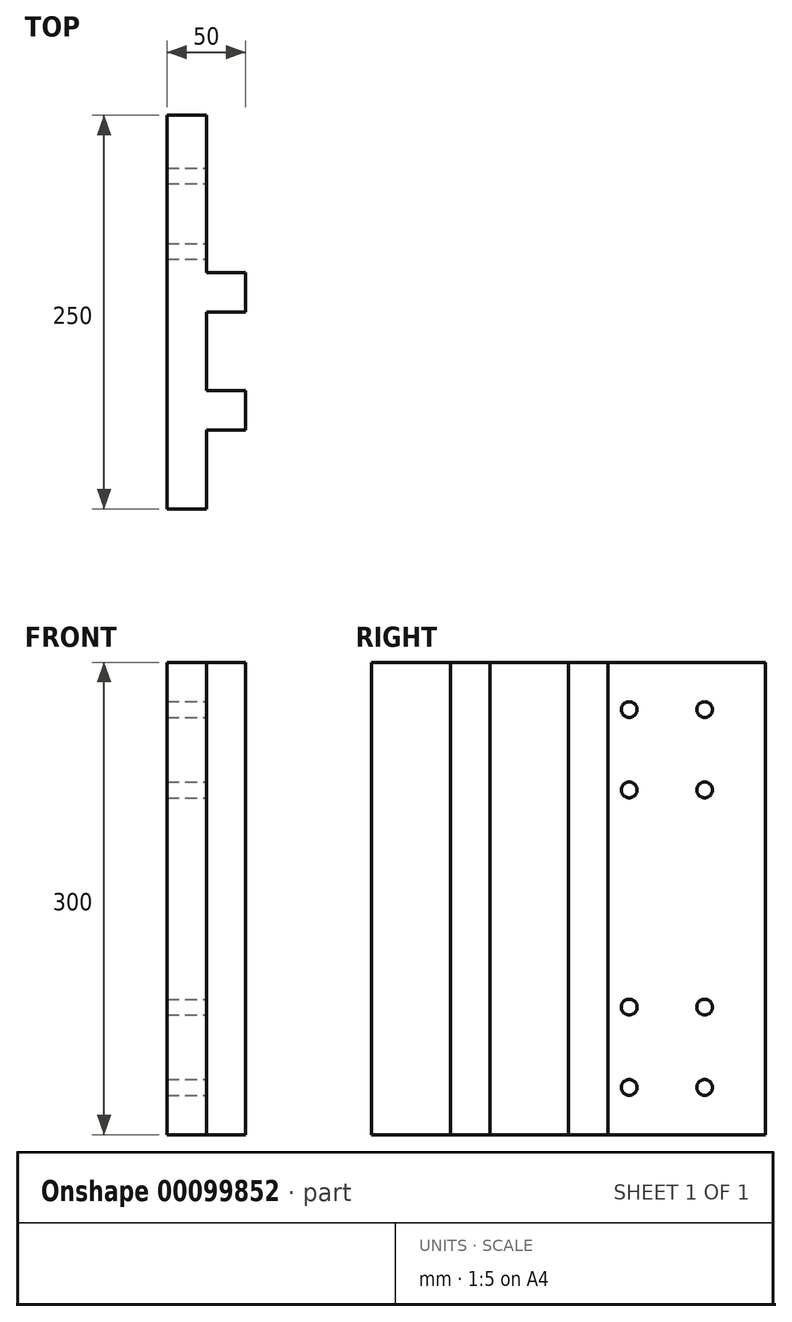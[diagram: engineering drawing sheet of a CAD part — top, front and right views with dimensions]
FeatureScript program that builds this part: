
annotation { "Feature Type Name" : "Feature", "Feature Type Description" : "" }
export const myFeature = defineFeature(function(context is Context, id is Id, definition is map)
    precondition{}
    {
        {
            var Q0;
            Q0=qCreatedBy(makeId("Right.planeOp"),FACE);
            var sketch = newSketch(context, id + "F0", { "sketchPlane" : qUnion([Q0])});
            skLineSegment(sketch, "E0.bottom", {"start": v(125, -150) * mm, "end": v(-125, -150) * mm});
            skLineSegment(sketch, "E0.top", {"start": v(125, 150) * mm, "end": v(-125, 150) * mm});
            skLineSegment(sketch, "E0.left", {"start": v(125, -150) * mm, "end": v(125, 150) * mm});
            skLineSegment(sketch, "E0.right", {"start": v(-125, -150) * mm, "end": v(-125, 150) * mm});
            skPoint(sketch, "E0.middle", {"position": v(0, 0) * mm});
            skSolve(sketch);
        }
        {
            var Q0;
            Q0 = qSketchRegion(id + "F0", true);
            extrude(context, id + "F1", {"entities" : qUnion([Q0]), "depth" : 25 * mm});
        }
        {
            var Q0;
            Q0=makeQuery(id+"F1.opExtrude","CAP_FACE",FACE,{"disambiguationData":[OSD([sQuery(id+"F0.wireOp",EDGE,"E0.bottom"),sQuery(id+"F0.wireOp",EDGE,"E0.top"),sQuery(id+"F0.wireOp",EDGE,"E0.left"),sQuery(id+"F0.wireOp",EDGE,"E0.right")])],"isStart":false});
            var sketch = newSketch(context, id + "F2", { "sketchPlane" : qUnion([Q0])});
            skLineSegment(sketch, "E1.top", {"start": v(-50, 150) * mm, "end": v(-75, 150) * mm});
            skLineSegment(sketch, "E1.left", {"start": v(-50, -150) * mm, "end": v(-50, 150) * mm});
            skLineSegment(sketch, "E1.right", {"start": v(-75, -150) * mm, "end": v(-75, 150) * mm});
            skLineSegment(sketch, "E2.trimOffspring", {"start": v(-50, -150) * mm, "end": v(-75, -150) * mm});
            skLineSegment(sketch, "E3.bottom", {"start": v(0, -150) * mm, "end": v(25, -150) * mm});
            skLineSegment(sketch, "E3.top", {"start": v(0, 150) * mm, "end": v(25, 150) * mm});
            skLineSegment(sketch, "E3.left", {"start": v(0, -150) * mm, "end": v(0, 150) * mm});
            skLineSegment(sketch, "E3.right", {"start": v(25, -150) * mm, "end": v(25, 150) * mm});
            skSolve(sketch);
        }
        {
            var Q0;
            Q0 = qSketchRegion(id + "F2", true);
            extrude(context, id + "F3", {"entities" : qUnion([Q0]), "operationType" : NewBodyOperationType.ADD, "depth" : 25 * mm});
        }
        {
            var Q0;
            {var subQ1=sQuery(id+"F0.wireOp",EDGE,"E0.right");var subQ3=sQuery(id+"F0.wireOp",EDGE,"E0.left");var subQ5=sQuery(id+"F0.wireOp",EDGE,"E0.top");Q0=makeQuery(id+"F3.boolean.opBoolean","SPLIT",FACE,{"disambiguationData":[TD([makeQuery(id+"F1.opExtrude","SWEPT_FACE",FACE,{"disambiguationData":[OSD([subQ5])]})])],"derivedFrom":makeQuery(id+"F1.opExtrude","CAP_FACE",FACE,{"disambiguationData":[OSD([sQuery(id+"F0.wireOp",EDGE,"E0.bottom"),subQ5,subQ3,subQ1])],"isStart":false})});}
            var sketch = newSketch(context, id + "F4", { "sketchPlane" : qUnion([Q0])});
            skLineSegment(sketch, "E4.bottom", {"start": v(86.46, 120) * mm, "end": v(38.54, 120) * mm, "construction": true});
            skLineSegment(sketch, "E4.top", {"start": v(86.46, 68.98) * mm, "end": v(38.54, 68.98) * mm, "construction": true});
            skLineSegment(sketch, "E4.left", {"start": v(86.46, 120) * mm, "end": v(86.46, 68.98) * mm, "construction": true});
            skLineSegment(sketch, "E4.right", {"start": v(38.54, 120) * mm, "end": v(38.54, 68.98) * mm, "construction": true});
            skPoint(sketch, "E4.middle", {"position": v(62.5, 94.5) * mm});
            skCircle(sketch, "E5", {"center": v(86.46, 120) * mm, "radius": 5 * mm});
            skCircle(sketch, "E6", {"center": v(38.54, 68.98) * mm, "radius": 5 * mm});
            skCircle(sketch, "E7", {"center": v(38.54, 120) * mm, "radius": 5 * mm});
            skCircle(sketch, "E8", {"center": v(86.46, 68.98) * mm, "radius": 5 * mm});
            skLineSegment(sketch, "E9", {"start": v(125, 0) * mm, "end": v(-125, 0) * mm, "construction": true});
            skPoint(sketch, "E9.endSnap0", {"position": v(-125, 0) * mm});
            skCircle(sketch, "E10.MirrorC", {"center": v(86.46, -68.98) * mm, "radius": 5 * mm});
            skCircle(sketch, "E11.MirrorC", {"center": v(86.46, -120) * mm, "radius": 5 * mm});
            skCircle(sketch, "E12.MirrorC", {"center": v(38.54, -120) * mm, "radius": 5 * mm});
            skCircle(sketch, "E13.MirrorC", {"center": v(38.54, -68.98) * mm, "radius": 5 * mm});
            skSolve(sketch);
        }
        {
            var Q0;
            Q0 = qSketchRegion(id + "F4", true);
            extrude(context, id + "F5", {"entities" : qUnion([Q0]), "operationType" : NewBodyOperationType.REMOVE, "endBound" : BoundingType.UP_TO_NEXT, "oppositeDirection" : true, "depth" : 25 * mm});
        }
    });
